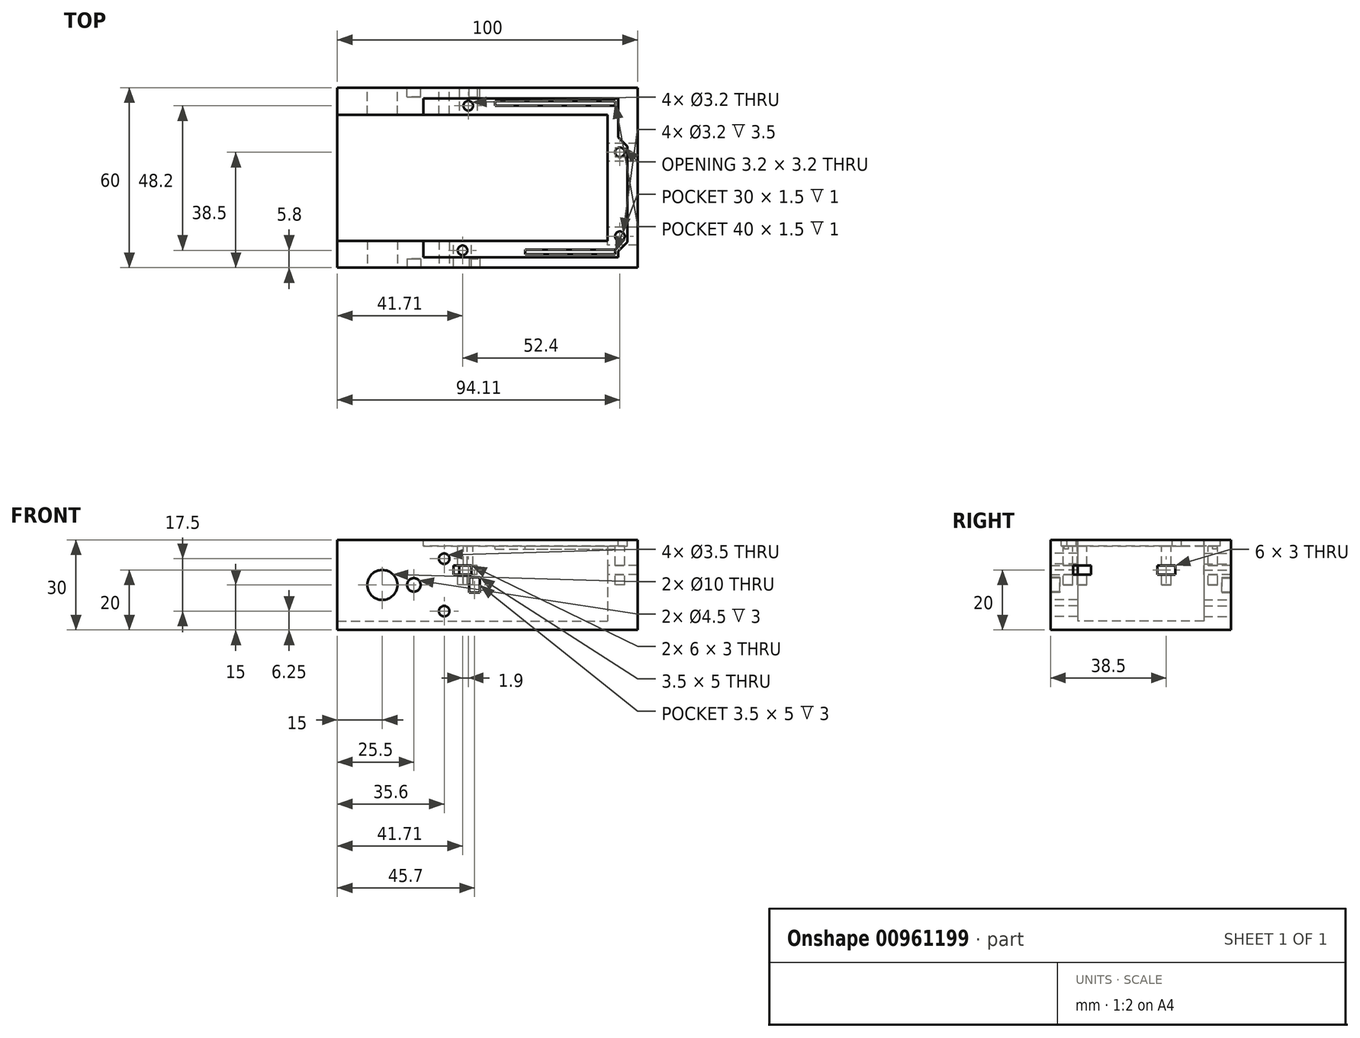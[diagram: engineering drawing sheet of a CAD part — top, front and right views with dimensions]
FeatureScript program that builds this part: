
annotation { "Feature Type Name" : "Feature", "Feature Type Description" : "" }
export const myFeature = defineFeature(function(context is Context, id is Id, definition is map)
    precondition{}
    {
        {
            var Q0;
            Q0=qCreatedBy(makeId("Top.planeOp"),FACE);
            var sketch = newSketch(context, id + "F0", { "sketchPlane" : qUnion([Q0])});
            skLineSegment(sketch, "E0.bottom", {"start": v(-50, 30) * mm, "end": v(50, 30) * mm});
            skLineSegment(sketch, "E0.top", {"start": v(-50, -30) * mm, "end": v(50, -30) * mm});
            skLineSegment(sketch, "E0.left", {"start": v(-50, 30) * mm, "end": v(-50, -30) * mm});
            skLineSegment(sketch, "E0.right", {"start": v(50, 30) * mm, "end": v(50, -30) * mm});
            skPoint(sketch, "E0.middle", {"position": v(0, 0) * mm});
            skLineSegment(sketch, "E1.bottom", {"start": v(-50, 21) * mm, "end": v(40, 21) * mm});
            skLineSegment(sketch, "E1.top", {"start": v(-50, -21) * mm, "end": v(40, -21) * mm});
            skLineSegment(sketch, "E1.left", {"start": v(-50, 21) * mm, "end": v(-50, -21) * mm});
            skLineSegment(sketch, "E1.right", {"start": v(40, 21) * mm, "end": v(40, -21) * mm});
            skSolve(sketch);
        }
        {
            var Q0;
            {var subQ4=sQuery(id+"F0.wireOp",EDGE,"E0.bottom");Q0=makeQuery(id+"F0.imprint","IMPRINT",FACE,{"disambiguationData":[TD([[makeQuery(id+"F0.imprint","IMPRINT",EDGE,{"derivedFrom":subQ4}),-1.0]])]});}
            extrude(context, id + "F1", {"entities" : qUnion([Q0]), "depth" : 30 * mm, "offsetDistance" : 25 * mm});
        }
        {
            var Q0;
            Q0=makeQuery(id+"F0.imprint","IMPRINT",FACE,{"disambiguationData":[TD([[makeQuery(id+"F0.imprint","IMPRINT",EDGE,{"derivedFrom":sQuery(id+"F0.wireOp",EDGE,"E1.bottom")}),-1.0]])]});
            extrude(context, id + "F2", {"entities" : qUnion([Q0]), "operationType" : NewBodyOperationType.ADD, "depth" : 3 * mm, "offsetDistance" : 25 * mm});
        }
        {
            var Q0;
            Q0=makeQuery(id+"F1.opExtrude","SWEPT_FACE",FACE,{"disambiguationData":[OSD([sQuery(id+"F0.wireOp",EDGE,"E0.top")])]});
            var sketch = newSketch(context, id + "F3", { "sketchPlane" : qUnion([Q0])});
            skCircle(sketch, "E2", {"center": v(-14.4, 23.75) * mm, "radius": 1.75 * mm});
            skCircle(sketch, "E3", {"center": v(-14.4, 6.25) * mm, "radius": 1.75 * mm});
            skLineSegment(sketch, "E4", {"start": v(-50, 15) * mm, "end": v(50, 15) * mm, "construction": true});
            skCircle(sketch, "E5", {"center": v(-35, 15) * mm, "radius": 5 * mm});
            skCircle(sketch, "E6", {"center": v(-24.5, 15) * mm, "radius": 2.25 * mm});
            skLineSegment(sketch, "E7.bottom", {"start": v(-6.05, 17.5) * mm, "end": v(-2.55, 17.5) * mm});
            skLineSegment(sketch, "E7.top", {"start": v(-6.05, 12.5) * mm, "end": v(-2.55, 12.5) * mm});
            skLineSegment(sketch, "E7.left", {"start": v(-6.05, 17.5) * mm, "end": v(-6.05, 12.5) * mm});
            skLineSegment(sketch, "E7.right", {"start": v(-2.55, 17.5) * mm, "end": v(-2.55, 12.5) * mm});
            skPoint(sketch, "E7.middle", {"position": v(-4.3, 15) * mm});
            skSolve(sketch);
        }
        {
            var Q0;
            Q0=makeQuery(id+"F3.imprint","IMPRINT",FACE,{"disambiguationData":[TD([[makeQuery(id+"F3.imprint","IMPRINT",EDGE,{"derivedFrom":sQuery(id+"F3.wireOp",EDGE,"E5")}),1.0]])]});
            var Q1;
            Q1=makeQuery(id+"F3.imprint","IMPRINT",FACE,{"disambiguationData":[TD([[makeQuery(id+"F3.imprint","IMPRINT",EDGE,{"derivedFrom":sQuery(id+"F3.wireOp",EDGE,"E2")}),1.0]])]});
            var Q2;
            Q2=makeQuery(id+"F3.imprint","IMPRINT",FACE,{"disambiguationData":[TD([[makeQuery(id+"F3.imprint","IMPRINT",EDGE,{"derivedFrom":sQuery(id+"F3.wireOp",EDGE,"E3")}),1.0]])]});
            extrude(context, id + "F4", {"entities" : qUnion([Q0, Q1, Q2]), "operationType" : NewBodyOperationType.REMOVE, "endBound" : BoundingType.UP_TO_NEXT, "oppositeDirection" : true, "depth" : 25 * mm, "offsetDistance" : 25 * mm});
        }
        {
            var Q0;
            Q0=makeQuery(id+"F3.imprint","IMPRINT",FACE,{"disambiguationData":[TD([[makeQuery(id+"F3.imprint","IMPRINT",EDGE,{"derivedFrom":sQuery(id+"F3.wireOp",EDGE,"E6")}),1.0]])]});
            var Q1;
            Q1=makeQuery(id+"F3.imprint","IMPRINT",FACE,{"disambiguationData":[TD([[makeQuery(id+"F3.imprint","IMPRINT",EDGE,{"derivedFrom":sQuery(id+"F3.wireOp",EDGE,"E7.bottom")}),-1.0]])]});
            extrude(context, id + "F5", {"entities" : qUnion([Q0, Q1]), "operationType" : NewBodyOperationType.REMOVE, "oppositeDirection" : true, "depth" : 3 * mm, "offsetDistance" : 25 * mm});
        }
        {
            var Q0;
            Q0=makeQuery(id+"F1.opExtrude","SWEPT_BODY",BODY,{"disambiguationData":[OSD([sQuery(id+"F0.wireOp",EDGE,"E0.bottom"),sQuery(id+"F0.wireOp",EDGE,"E0.top"),sQuery(id+"F0.wireOp",EDGE,"E0.left"),sQuery(id+"F0.wireOp",EDGE,"E0.right"),sQuery(id+"F0.wireOp",EDGE,"E1.bottom"),sQuery(id+"F0.wireOp",EDGE,"E1.top"),sQuery(id+"F0.wireOp",EDGE,"E1.right")])]});
            var Q1;
            Q1=qCreatedBy(makeId("Front.planeOp"),FACE);
            mirror(context, id + "F6", {"operationType" : NewBodyOperationType.INTERSECT, "entities" : qUnion([Q0]), "mirrorPlane" : qUnion([Q1])});
        }
        {
            var Q0;
            Q0=makeQuery(id+"F1.opExtrude","CAP_FACE",FACE,{"disambiguationData":[OSD([sQuery(id+"F0.wireOp",EDGE,"E0.bottom"),sQuery(id+"F0.wireOp",EDGE,"E0.top"),sQuery(id+"F0.wireOp",EDGE,"E0.left"),sQuery(id+"F0.wireOp",EDGE,"E0.right"),sQuery(id+"F0.wireOp",EDGE,"E1.bottom"),sQuery(id+"F0.wireOp",EDGE,"E1.top"),sQuery(id+"F0.wireOp",EDGE,"E1.right")])],"isStart":false});
            var sketch = newSketch(context, id + "F7", { "sketchPlane" : qUnion([Q0])});
            skLineSegment(sketch, "E8", {"start": v(-21.39, 26.5) * mm, "end": v(-21.39, -26.5) * mm});
            skLineSegment(sketch, "E9", {"start": v(-21.39, -26.5) * mm, "end": v(43.61, -26.5) * mm});
            skLineSegment(sketch, "E10", {"start": v(43.61, -26.5) * mm, "end": v(43.61, -24.5) * mm});
            skLineSegment(sketch, "E11", {"start": v(43.61, -24.5) * mm, "end": v(46.61, -21.5) * mm});
            skLineSegment(sketch, "E12", {"start": v(46.61, -21.5) * mm, "end": v(46.61, 10.5) * mm});
            skLineSegment(sketch, "E13", {"start": v(46.61, 10.5) * mm, "end": v(43.61, 13.5) * mm});
            skLineSegment(sketch, "E14", {"start": v(43.61, 13.5) * mm, "end": v(43.61, 26.5) * mm});
            skLineSegment(sketch, "E15", {"start": v(43.61, 26.5) * mm, "end": v(-21.39, 26.5) * mm});
            skLineSegment(sketch, "E16.bottom", {"start": v(2.61, 25.5) * mm, "end": v(42.61, 25.5) * mm});
            skLineSegment(sketch, "E16.top", {"start": v(2.61, 24) * mm, "end": v(42.61, 24) * mm});
            skLineSegment(sketch, "E16.left", {"start": v(2.61, 25.5) * mm, "end": v(2.61, 24) * mm});
            skLineSegment(sketch, "E16.right", {"start": v(42.61, 25.5) * mm, "end": v(42.61, 24) * mm});
            skLineSegment(sketch, "E17.bottom", {"start": v(12.61, -24) * mm, "end": v(42.61, -24) * mm});
            skLineSegment(sketch, "E17.top", {"start": v(12.61, -25.5) * mm, "end": v(42.61, -25.5) * mm});
            skLineSegment(sketch, "E17.left", {"start": v(12.61, -24) * mm, "end": v(12.61, -25.5) * mm});
            skLineSegment(sketch, "E17.right", {"start": v(42.61, -24) * mm, "end": v(42.61, -25.5) * mm});
            skCircle(sketch, "E18", {"center": v(-6.39, 24) * mm, "radius": 1.6 * mm});
            skCircle(sketch, "E19", {"center": v(-8.29, -24.2) * mm, "radius": 1.6 * mm});
            skCircle(sketch, "E20", {"center": v(44.11, 8.5) * mm, "radius": 1.6 * mm});
            skCircle(sketch, "E21", {"center": v(44.11, -19.5) * mm, "radius": 1.6 * mm});
            skLineSegment(sketch, "E22", {"start": v(-6.39, 24) * mm, "end": v(-6.39, 21) * mm, "construction": true});
            skSolve(sketch);
        }
        {
            var Q0;
            Q0=makeQuery(id+"F7.imprint","IMPRINT",FACE,{"disambiguationData":[TD([[makeQuery(id+"F7.imprint","IMPRINT",EDGE,{"derivedFrom":sQuery(id+"F7.wireOp",EDGE,"E16.bottom")}),-1.0]])]});
            var Q1;
            Q1=makeQuery(id+"F7.imprint","IMPRINT",FACE,{"disambiguationData":[TD([[makeQuery(id+"F7.imprint","IMPRINT",EDGE,{"derivedFrom":sQuery(id+"F7.wireOp",EDGE,"E17.bottom")}),-1.0]])]});
            extrude(context, id + "F8", {"entities" : qUnion([Q0, Q1]), "operationType" : NewBodyOperationType.REMOVE, "oppositeDirection" : true, "depth" : 3 * mm, "offsetDistance" : 25 * mm});
        }
        {
            var Q0;
            Q0 = qSketchRegion(id + "F7", true);
            extrude(context, id + "F9", {"entities" : qUnion([Q0]), "operationType" : NewBodyOperationType.REMOVE, "oppositeDirection" : true, "depth" : 2 * mm, "offsetDistance" : 25 * mm});
        }
        {
            var Q0;
            Q0=makeQuery(id+"F9.boolean.opBoolean","SPLIT",FACE,{"disambiguationData":[TD([makeQuery(id+"F9.opExtrude","SWEPT_FACE",FACE,{"disambiguationData":[OSD([sQuery(id+"F7.wireOp",EDGE,"E18")])]})])],"derivedFrom":makeQuery(id+"F1.opExtrude","CAP_FACE",FACE,{"disambiguationData":[OSD([sQuery(id+"F0.wireOp",EDGE,"E0.bottom"),sQuery(id+"F0.wireOp",EDGE,"E0.top"),sQuery(id+"F0.wireOp",EDGE,"E0.left"),sQuery(id+"F0.wireOp",EDGE,"E0.right"),sQuery(id+"F0.wireOp",EDGE,"E1.bottom"),sQuery(id+"F0.wireOp",EDGE,"E1.top"),sQuery(id+"F0.wireOp",EDGE,"E1.right")])],"isStart":false})});
            var Q1;
            Q1=makeQuery(id+"F9.boolean.opBoolean","SPLIT",FACE,{"disambiguationData":[TD([makeQuery(id+"F9.opExtrude","SWEPT_FACE",FACE,{"disambiguationData":[OSD([sQuery(id+"F7.wireOp",EDGE,"E20")])]})])],"derivedFrom":makeQuery(id+"F1.opExtrude","CAP_FACE",FACE,{"disambiguationData":[OSD([sQuery(id+"F0.wireOp",EDGE,"E0.bottom"),sQuery(id+"F0.wireOp",EDGE,"E0.top"),sQuery(id+"F0.wireOp",EDGE,"E0.left"),sQuery(id+"F0.wireOp",EDGE,"E0.right"),sQuery(id+"F0.wireOp",EDGE,"E1.bottom"),sQuery(id+"F0.wireOp",EDGE,"E1.top"),sQuery(id+"F0.wireOp",EDGE,"E1.right")])],"isStart":false})});
            var Q2;
            Q2=makeQuery(id+"F9.boolean.opBoolean","SPLIT",FACE,{"disambiguationData":[TD([makeQuery(id+"F9.opExtrude","SWEPT_FACE",FACE,{"disambiguationData":[OSD([sQuery(id+"F7.wireOp",EDGE,"E21")])]})])],"derivedFrom":makeQuery(id+"F1.opExtrude","CAP_FACE",FACE,{"disambiguationData":[OSD([sQuery(id+"F0.wireOp",EDGE,"E0.bottom"),sQuery(id+"F0.wireOp",EDGE,"E0.top"),sQuery(id+"F0.wireOp",EDGE,"E0.left"),sQuery(id+"F0.wireOp",EDGE,"E0.right"),sQuery(id+"F0.wireOp",EDGE,"E1.bottom"),sQuery(id+"F0.wireOp",EDGE,"E1.top"),sQuery(id+"F0.wireOp",EDGE,"E1.right")])],"isStart":false})});
            var Q3;
            Q3=makeQuery(id+"F9.boolean.opBoolean","SPLIT",FACE,{"disambiguationData":[TD([makeQuery(id+"F9.opExtrude","SWEPT_FACE",FACE,{"disambiguationData":[OSD([sQuery(id+"F7.wireOp",EDGE,"E19")])]})])],"derivedFrom":makeQuery(id+"F1.opExtrude","CAP_FACE",FACE,{"disambiguationData":[OSD([sQuery(id+"F0.wireOp",EDGE,"E0.bottom"),sQuery(id+"F0.wireOp",EDGE,"E0.top"),sQuery(id+"F0.wireOp",EDGE,"E0.left"),sQuery(id+"F0.wireOp",EDGE,"E0.right"),sQuery(id+"F0.wireOp",EDGE,"E1.bottom"),sQuery(id+"F0.wireOp",EDGE,"E1.top"),sQuery(id+"F0.wireOp",EDGE,"E1.right")])],"isStart":false})});
            extrude(context, id + "F10", {"entities" : qUnion([Q0, Q1, Q2, Q3]), "operationType" : NewBodyOperationType.REMOVE, "oppositeDirection" : true, "depth" : 15 * mm, "offsetDistance" : 25 * mm});
        }
        {
            var Q0;
            Q0=makeQuery(id+"F1.opExtrude","SWEPT_FACE",FACE,{"disambiguationData":[OSD([sQuery(id+"F0.wireOp",EDGE,"E1.bottom")])]});
            var sketch = newSketch(context, id + "F11", { "sketchPlane" : qUnion([Q0])});
            skLineSegment(sketch, "E23.bottom", {"start": v(-3.39, 18.5) * mm, "end": v(-9.39, 18.5) * mm});
            skLineSegment(sketch, "E23.top", {"start": v(-3.39, 21.5) * mm, "end": v(-9.39, 21.5) * mm});
            skLineSegment(sketch, "E23.left", {"start": v(-3.39, 18.5) * mm, "end": v(-3.39, 21.5) * mm});
            skLineSegment(sketch, "E23.right", {"start": v(-9.39, 18.5) * mm, "end": v(-9.39, 21.5) * mm});
            skLineSegment(sketch, "E24", {"start": v(-6.39, 24.16) * mm, "end": v(-6.39, 30) * mm, "construction": true});
            skSolve(sketch);
        }
        {
            var Q0;
            Q0 = qSketchRegion(id + "F11", true);
            var Q1;
            Q1=makeQuery(id+"F1.opExtrude","SWEPT_FACE",FACE,{"disambiguationData":[OSD([sQuery(id+"F0.wireOp",EDGE,"E0.bottom")])]});
            extrude(context, id + "F12", {"entities" : qUnion([Q0]), "operationType" : NewBodyOperationType.REMOVE, "endBound" : BoundingType.UP_TO_SURFACE, "oppositeDirection" : true, "depth" : 8 * mm, "endBoundEntityFace" : qUnion([Q1]), "offsetDistance" : 25 * mm});
        }
        {
            var Q0;
            Q0=makeQuery(id+"F1.opExtrude","SWEPT_FACE",FACE,{"disambiguationData":[OSD([sQuery(id+"F0.wireOp",EDGE,"E1.top")])]});
            var sketch = newSketch(context, id + "F13", { "sketchPlane" : qUnion([Q0])});
            skLineSegment(sketch, "E25", {"start": v(8.29, 30) * mm, "end": v(8.29, 21.5) * mm, "construction": true});
            skLineSegment(sketch, "E26.bottom", {"start": v(11.29, 18.5) * mm, "end": v(5.29, 18.5) * mm});
            skLineSegment(sketch, "E26.top", {"start": v(11.29, 21.5) * mm, "end": v(5.29, 21.5) * mm});
            skLineSegment(sketch, "E26.left", {"start": v(11.29, 18.5) * mm, "end": v(11.29, 21.5) * mm});
            skLineSegment(sketch, "E26.right", {"start": v(5.29, 18.5) * mm, "end": v(5.29, 21.5) * mm});
            skSolve(sketch);
        }
        {
            var Q0;
            Q0 = qSketchRegion(id + "F13", true);
            var Q1;
            Q1=makeQuery(id+"F1.opExtrude","SWEPT_FACE",FACE,{"disambiguationData":[OSD([sQuery(id+"F0.wireOp",EDGE,"E0.top")])]});
            extrude(context, id + "F14", {"entities" : qUnion([Q0]), "operationType" : NewBodyOperationType.REMOVE, "endBound" : BoundingType.UP_TO_SURFACE, "oppositeDirection" : true, "depth" : 25 * mm, "endBoundEntityFace" : qUnion([Q1]), "offsetDistance" : 25 * mm});
        }
        {
            var Q0;
            Q0=makeQuery(id+"F1.opExtrude","SWEPT_FACE",FACE,{"disambiguationData":[OSD([sQuery(id+"F0.wireOp",EDGE,"E1.right")])]});
            var sketch = newSketch(context, id + "F15", { "sketchPlane" : qUnion([Q0])});
            skLineSegment(sketch, "E27", {"start": v(-8.5, 30) * mm, "end": v(-8.5, 10.58) * mm, "construction": true});
            skLineSegment(sketch, "E28", {"start": v(19.5, 30) * mm, "end": v(19.5, 9.55) * mm, "construction": true});
            skLineSegment(sketch, "E29.bottom", {"start": v(-11.5, 21.5) * mm, "end": v(-5.5, 21.5) * mm});
            skLineSegment(sketch, "E29.top", {"start": v(-11.5, 18.5) * mm, "end": v(-5.5, 18.5) * mm});
            skLineSegment(sketch, "E29.left", {"start": v(-11.5, 21.5) * mm, "end": v(-11.5, 18.5) * mm});
            skLineSegment(sketch, "E29.right", {"start": v(-5.5, 21.5) * mm, "end": v(-5.5, 18.5) * mm});
            skLineSegment(sketch, "E30.bottom", {"start": v(22.5, 21.5) * mm, "end": v(16.5, 21.5) * mm});
            skLineSegment(sketch, "E30.top", {"start": v(22.5, 18.5) * mm, "end": v(16.5, 18.5) * mm});
            skLineSegment(sketch, "E30.left", {"start": v(22.5, 21.5) * mm, "end": v(22.5, 18.5) * mm});
            skLineSegment(sketch, "E30.right", {"start": v(16.5, 21.5) * mm, "end": v(16.5, 18.5) * mm});
            skSolve(sketch);
        }
        {
            var Q0;
            Q0 = qSketchRegion(id + "F15", true);
            var Q1;
            Q1=makeQuery(id+"F1.opExtrude","SWEPT_FACE",FACE,{"disambiguationData":[OSD([sQuery(id+"F0.wireOp",EDGE,"E0.right")])]});
            extrude(context, id + "F16", {"entities" : qUnion([Q0]), "operationType" : NewBodyOperationType.REMOVE, "endBound" : BoundingType.UP_TO_SURFACE, "oppositeDirection" : true, "depth" : 25 * mm, "endBoundEntityFace" : qUnion([Q1]), "offsetDistance" : 25 * mm});
        }
    });
